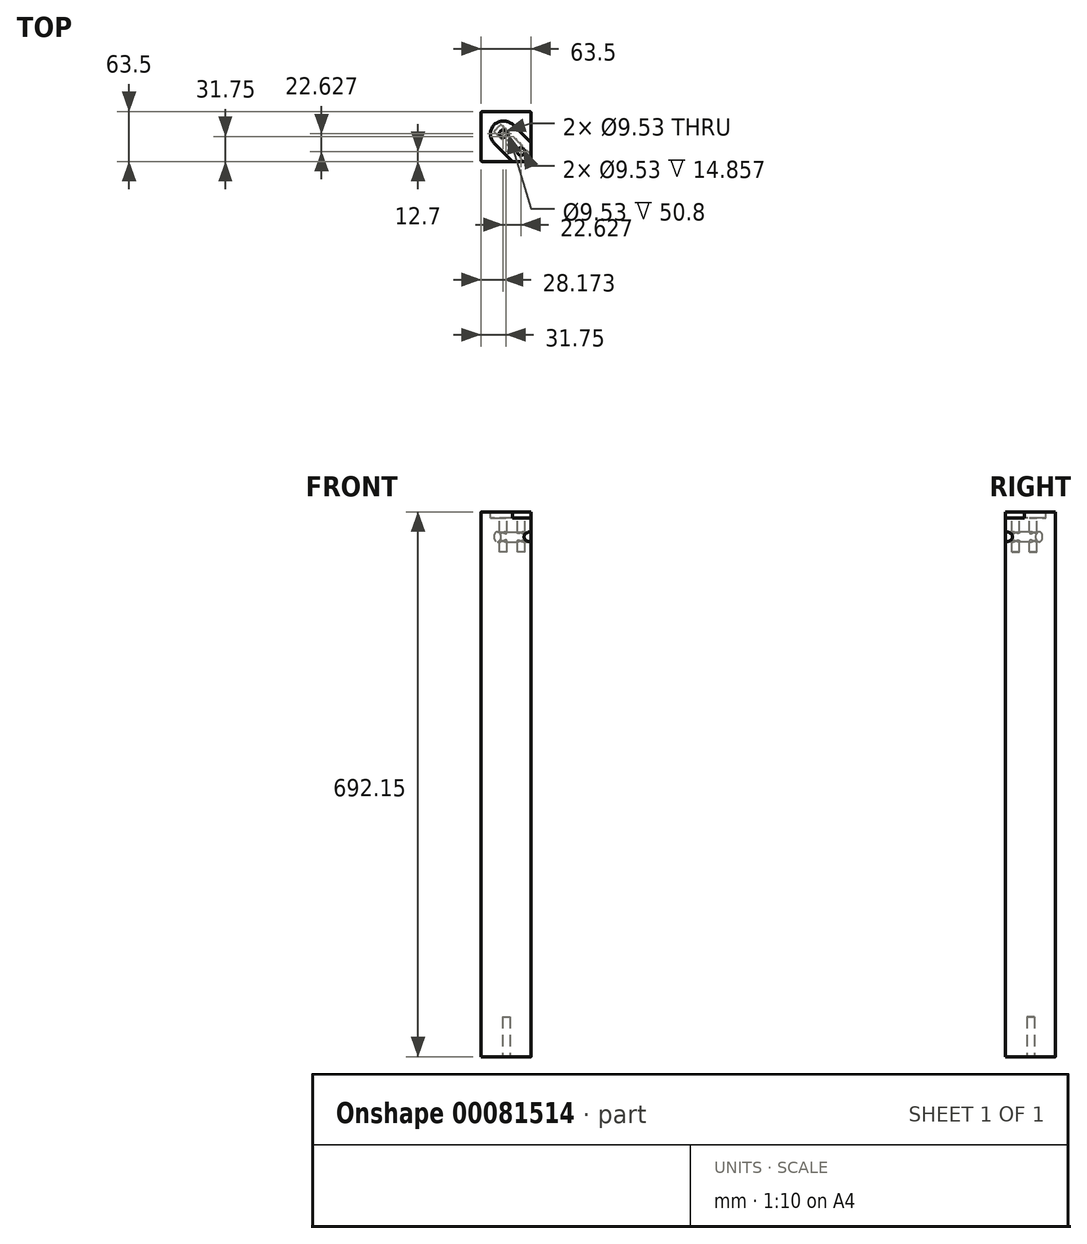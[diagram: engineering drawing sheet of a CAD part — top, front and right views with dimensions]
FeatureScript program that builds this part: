
annotation { "Feature Type Name" : "Feature", "Feature Type Description" : "" }
export const myFeature = defineFeature(function(context is Context, id is Id, definition is map)
    precondition{}
    {
        {
            var Q0;
            Q0=qCreatedBy(makeId("Top.planeOp"),FACE);
            var sketch = newSketch(context, id + "F0", { "sketchPlane" : qUnion([Q0])});
            skLineSegment(sketch, "E0.bottom", {"start": v(31.75, -31.75) * mm, "end": v(-31.75, -31.75) * mm});
            skLineSegment(sketch, "E0.top", {"start": v(31.75, 31.75) * mm, "end": v(-31.75, 31.75) * mm});
            skLineSegment(sketch, "E0.left", {"start": v(31.75, -31.75) * mm, "end": v(31.75, 31.75) * mm});
            skLineSegment(sketch, "E0.right", {"start": v(-31.75, -31.75) * mm, "end": v(-31.75, 31.75) * mm});
            skPoint(sketch, "E0.middle", {"position": v(0, 0) * mm});
            skSolve(sketch);
        }
        {
            var Q0;
            Q0=makeQuery(id+"F0.imprint","IMPRINT",FACE,{"disambiguationData":[TD([[makeQuery(id+"F0.imprint","IMPRINT",EDGE,{"derivedFrom":sQuery(id+"F0.wireOp",EDGE,"E0.bottom")}),-1.0]])]});
            extrude(context, id + "F1", {"entities" : qUnion([Q0]), "oppositeDirection" : true, "depth" : 692.15 * mm});
        }
        {
            var Q0;
            Q0=makeQuery(id+"F1.opExtrude","CAP_FACE",FACE,{"disambiguationData":[OSD([sQuery(id+"F0.wireOp",EDGE,"E0.bottom"),sQuery(id+"F0.wireOp",EDGE,"E0.top"),sQuery(id+"F0.wireOp",EDGE,"E0.left"),sQuery(id+"F0.wireOp",EDGE,"E0.right")])],"isStart":true});
            var sketch = newSketch(context, id + "F2", { "sketchPlane" : qUnion([Q0])});
            skLineSegment(sketch, "E1", {"start": v(31.75, -31.75) * mm, "end": v(-31.75, 31.75) * mm, "construction": true});
            skCircle(sketch, "E2", {"center": v(19.05, -19.05) * mm, "radius": 4.76 * mm});
            skCircle(sketch, "E3", {"center": v(-3.58, 3.58) * mm, "radius": 4.76 * mm});
            skSolve(sketch);
        }
        {
            var Q0;
            Q0=makeQuery(id+"F2.imprint","IMPRINT",FACE,{"disambiguationData":[TD([[makeQuery(id+"F2.imprint","IMPRINT",EDGE,{"derivedFrom":sQuery(id+"F2.wireOp",EDGE,"E3")}),1.0]])]});
            var Q1;
            Q1=makeQuery(id+"F2.imprint","IMPRINT",FACE,{"disambiguationData":[TD([[makeQuery(id+"F2.imprint","IMPRINT",EDGE,{"derivedFrom":sQuery(id+"F2.wireOp",EDGE,"E2")}),1.0]])]});
            extrude(context, id + "F3", {"entities" : qUnion([Q0, Q1]), "operationType" : NewBodyOperationType.REMOVE, "oppositeDirection" : true, "depth" : 50.8 * mm});
        }
        {
            var Q0;
            Q0=makeQuery(id+"F1.opExtrude","SWEPT_EDGE",EDGE,{"disambiguationData":[OSD([sQuery(id+"F0.wireOp",EDGE,"E0.bottom"),sQuery(id+"F0.wireOp",EDGE,"E0.left")])]});
            var Q1;
            Q1=makeQuery(id+"F1.opExtrude","CAP_EDGE",EDGE,{"disambiguationData":[OSD([sQuery(id+"F0.wireOp",EDGE,"E0.left")])],"isStart":true});
            cPlane(context, id + "F4", {"entities" : qUnion([Q0, Q1]), "cplaneType" : CPlaneType.LINE_ANGLE, "offset" : 31.75 * mm, "angle" : 135 * degree, "width" : 152.4 * mm, "height" : 152.4 * mm});
        }
        {
            var Q0;
            Q0=qCreatedBy(id+"F4.planeOp",FACE);
            var sketch = newSketch(context, id + "F5", { "sketchPlane" : qUnion([Q0])});
            skCircle(sketch, "E4", {"center": v(0, -31.75) * mm, "radius": 6.35 * mm});
            skLineSegment(sketch, "E5.0", {"start": v(0, -692.15) * mm, "end": v(0, 0) * mm, "construction": true});
            skSolve(sketch);
        }
        {
            var Q0;
            Q0=makeQuery(id+"F5.imprint","IMPRINT",FACE,{"disambiguationData":[TD([[makeQuery(id+"F5.imprint","IMPRINT",EDGE,{"derivedFrom":sQuery(id+"F5.wireOp",EDGE,"E4")}),1.0]])]});
            var Q1;
            Q1=sQuery(id+"F5.wireOp",EDGE,"E4");
            extrude(context, id + "F6", {"entities" : qUnion([Q0]), "operationType" : NewBodyOperationType.REMOVE, "surfaceEntities" : qUnion([Q1]), "oppositeDirection" : true, "depth" : 60.32 * mm});
        }
        {
            var Q0;
            Q0=makeQuery(id+"F1.opExtrude","SWEPT_EDGE",EDGE,{"disambiguationData":[OSD([sQuery(id+"F0.wireOp",EDGE,"E0.bottom"),sQuery(id+"F0.wireOp",EDGE,"E0.right")])]});
            var Q1;
            Q1=makeQuery(id+"F1.opExtrude","SWEPT_EDGE",EDGE,{"disambiguationData":[OSD([sQuery(id+"F0.wireOp",EDGE,"E0.top"),sQuery(id+"F0.wireOp",EDGE,"E0.right")])]});
            var Q2;
            {var subQ0=sQuery(id+"F0.wireOp",EDGE,"E0.bottom");var subQ1=sQuery(id+"F0.wireOp",EDGE,"E0.left");Q2=makeQuery(id+"F6.boolean.opBoolean","SPLIT",EDGE,{"disambiguationData":[TD([makeQuery(id+"F1.opExtrude","CAP_FACE",FACE,{"disambiguationData":[OSD([subQ0,sQuery(id+"F0.wireOp",EDGE,"E0.top"),subQ1,sQuery(id+"F0.wireOp",EDGE,"E0.right")])],"isStart":true})])],"derivedFrom":makeQuery(id+"F1.opExtrude","SWEPT_EDGE",EDGE,{"disambiguationData":[OSD([subQ0,subQ1])]})});}
            var Q3;
            {var subQ0=sQuery(id+"F0.wireOp",EDGE,"E0.bottom");var subQ1=sQuery(id+"F0.wireOp",EDGE,"E0.left");Q3=makeQuery(id+"F6.boolean.opBoolean","SPLIT",EDGE,{"disambiguationData":[TD([makeQuery(id+"F1.opExtrude","CAP_FACE",FACE,{"disambiguationData":[OSD([subQ0,sQuery(id+"F0.wireOp",EDGE,"E0.top"),subQ1,sQuery(id+"F0.wireOp",EDGE,"E0.right")])],"isStart":false})])],"derivedFrom":makeQuery(id+"F1.opExtrude","SWEPT_EDGE",EDGE,{"disambiguationData":[OSD([subQ0,subQ1])]})});}
            var Q4;
            Q4=makeQuery(id+"F1.opExtrude","SWEPT_EDGE",EDGE,{"disambiguationData":[OSD([sQuery(id+"F0.wireOp",EDGE,"E0.top"),sQuery(id+"F0.wireOp",EDGE,"E0.left")])]});
            fillet(context, id + "F7", {"entities" : qUnion([Q0, Q1, Q2, Q3, Q4]), "radius" : 1.59 * mm, "tangentPropagation" : true, "allowEdgeOverflow" : false});
        }
        {
            var Q0;
            Q0=makeQuery(id+"F1.opExtrude","CAP_FACE",FACE,{"disambiguationData":[OSD([sQuery(id+"F0.wireOp",EDGE,"E0.bottom"),sQuery(id+"F0.wireOp",EDGE,"E0.top"),sQuery(id+"F0.wireOp",EDGE,"E0.left"),sQuery(id+"F0.wireOp",EDGE,"E0.right")])],"isStart":false});
            var sketch = newSketch(context, id + "F8", { "sketchPlane" : qUnion([Q0])});
            skCircle(sketch, "E6", {"center": v(0, 0) * mm, "radius": 4.76 * mm});
            skSolve(sketch);
        }
        {
            var Q0;
            Q0=makeQuery(id+"F8.imprint","IMPRINT",FACE,{"disambiguationData":[TD([[makeQuery(id+"F8.imprint","IMPRINT",EDGE,{"derivedFrom":sQuery(id+"F8.wireOp",EDGE,"E6")}),1.0]])]});
            extrude(context, id + "F9", {"entities" : qUnion([Q0]), "operationType" : NewBodyOperationType.REMOVE, "oppositeDirection" : true, "depth" : 50.8 * mm});
        }
        {
            var Q0;
            Q0=makeQuery(id+"F1.opExtrude","CAP_FACE",FACE,{"disambiguationData":[OSD([sQuery(id+"F0.wireOp",EDGE,"E0.bottom"),sQuery(id+"F0.wireOp",EDGE,"E0.top"),sQuery(id+"F0.wireOp",EDGE,"E0.left"),sQuery(id+"F0.wireOp",EDGE,"E0.right")])],"isStart":true});
            var sketch = newSketch(context, id + "F10", { "sketchPlane" : qUnion([Q0])});
            skArc(sketch, "E7", {"start": v(8.55, 15.02) * mm, "mid": v(-14.96, 14.96) * mm, "end": v(-15.02, -8.55) * mm});
            skLineSegment(sketch, "E8", {"start": v(-15.02, -8.55) * mm, "end": v(7.94, -31.75) * mm});
            skLineSegment(sketch, "E9", {"start": v(8.55, 15.02) * mm, "end": v(31.75, -7.94) * mm});
            skArc(sketch, "E10.0", {"start": v(30.16, -31.75) * mm, "mid": v(31.29, -31.29) * mm, "end": v(31.75, -30.16) * mm});
            skLineSegment(sketch, "E11.0", {"start": v(30.16, -31.75) * mm, "end": v(7.94, -31.75) * mm});
            skLineSegment(sketch, "E12.0", {"start": v(31.75, -30.16) * mm, "end": v(31.75, -7.94) * mm});
            skPoint(sketch, "E13.orphan", {"position": v(31.75, 30.16) * mm});
            skPoint(sketch, "E14.orphan", {"position": v(-30.16, -31.75) * mm});
            skSolve(sketch);
        }
        {
            var Q0;
            Q0=makeQuery(id+"F10.imprint","IMPRINT",FACE,{"disambiguationData":[TD([[makeQuery(id+"F10.imprint","IMPRINT",EDGE,{"derivedFrom":sQuery(id+"F10.wireOp",EDGE,"E7")}),1.0]])]});
            extrude(context, id + "F11", {"entities" : qUnion([Q0]), "operationType" : NewBodyOperationType.REMOVE, "oppositeDirection" : true, "depth" : 7.94 * mm});
        }
    });
